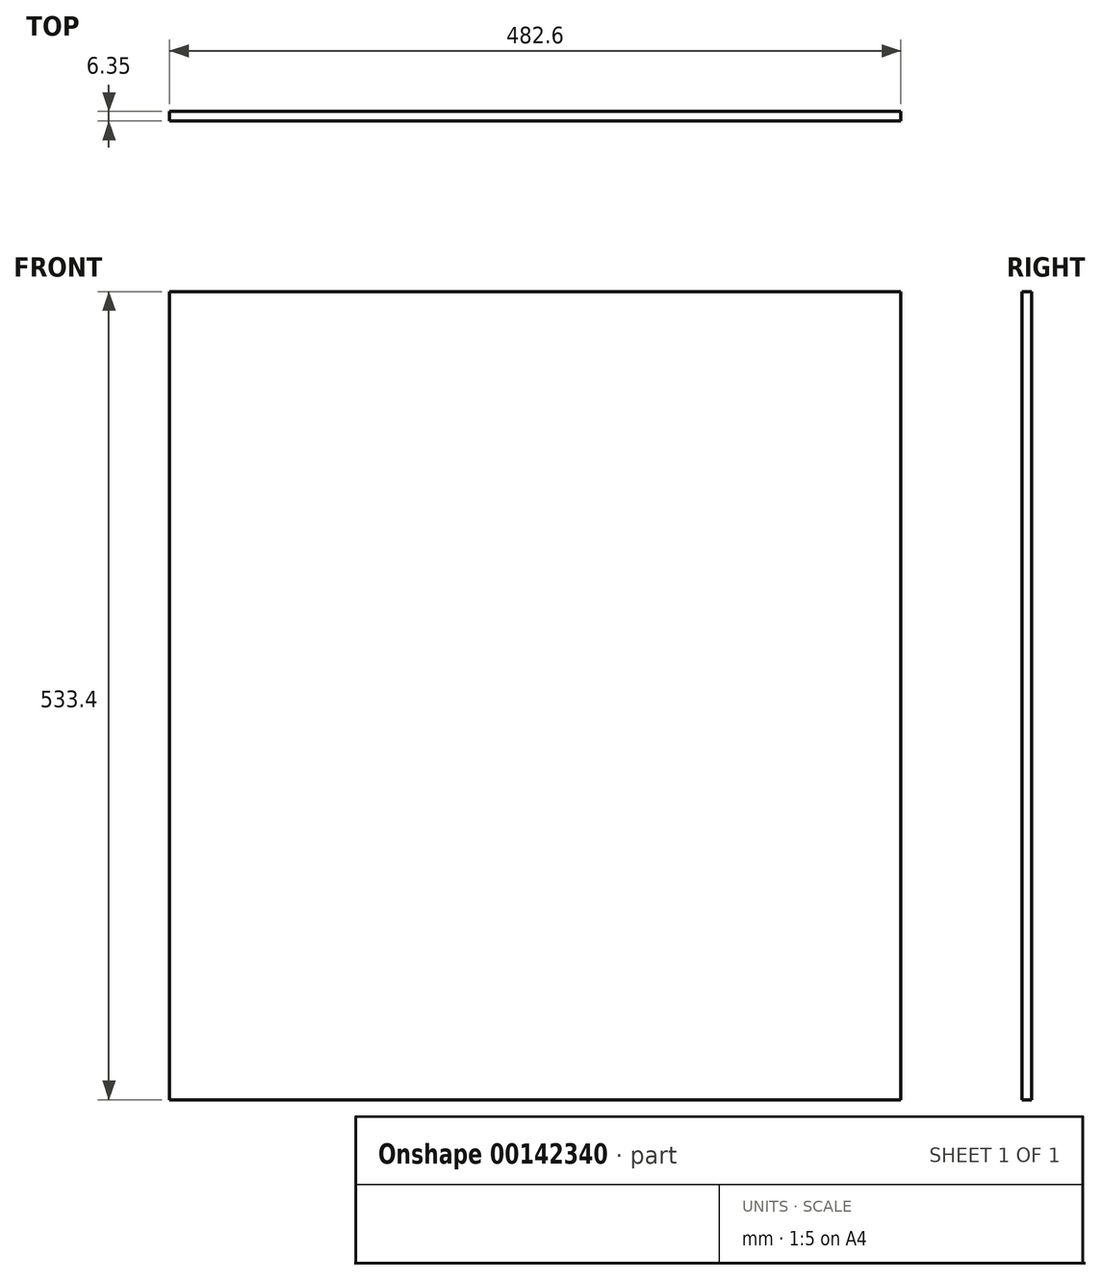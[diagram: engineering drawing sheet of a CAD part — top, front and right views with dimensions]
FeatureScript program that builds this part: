
annotation { "Feature Type Name" : "Feature", "Feature Type Description" : "" }
export const myFeature = defineFeature(function(context is Context, id is Id, definition is map)
    precondition{}
    {
        {
            var Q0;
            Q0=qCreatedBy(makeId("Front.planeOp"),FACE);
            var sketch = newSketch(context, id + "F0", { "sketchPlane" : qUnion([Q0])});
            skLineSegment(sketch, "E0.bottom", {"start": v(-239.53, 283.63) * mm, "end": v(243.07, 283.63) * mm});
            skLineSegment(sketch, "E0.top", {"start": v(-239.53, -249.77) * mm, "end": v(243.07, -249.77) * mm});
            skLineSegment(sketch, "E0.left", {"start": v(-239.53, 283.63) * mm, "end": v(-239.53, -249.77) * mm});
            skLineSegment(sketch, "E0.right", {"start": v(243.07, 283.63) * mm, "end": v(243.07, -249.77) * mm});
            skSolve(sketch);
        }
        {
            var Q0;
            Q0=makeQuery(id+"F0.imprint","IMPRINT",FACE,{"disambiguationData":[TD([[makeQuery(id+"F0.imprint","IMPRINT",EDGE,{"derivedFrom":sQuery(id+"F0.wireOp",EDGE,"E0.bottom")}),-1.0]])]});
            extrude(context, id + "F1", {"entities" : qUnion([Q0]), "depth" : 6.35 * mm});
        }
    });
